# Revit family: 201_MAK+KL-_+TAK-___
name_source: partatom
category: Air Terminals
units: mm (PartAtom-declared; Revit-internal decimal feet)

## family parameters
Always vertical = Yes
Cut with Voids When Loaded = No
Part Type = Normal
Room Calculation Point = Yes
Round Connector Dimension = Use Diameter
Shared = No
Work Plane-Based = No

## types (4) — shared parameters
AA1 = 298 mm
AA2 = 298 mm
BOX0 = No
BOX1 = Yes
CAT0 = Yes
CAT1 = Yes
CAT2 = Yes
Description = Square nozzle diffuser with balancing plenum box
H4 = 8 mm  [stored 0.0262467 ft]
H4__ve = -8 mm  [stored -0.0262467 ft]
H5 = 10 mm  [stored 0.0328084 ft]
L_ARR = 400 mm
Manufacturer = Climecon
QmdConnectorList = 201;D
URL = www.climecon.fi
W_ARR = 400 mm
XRefLineVPlnId = 7453
YRefLineVPlnId = 7456
magiPartTypeId = 201
magiProductFamilyId = MAK+KL-*+TAK-*/*
zero-valued in all types: H_ARR, MC_Default_elevation

## per-type parameters (varying)
| type | B | B1 | B__ve | C | CLBTZ | CLBTZ_End__ve | CLBTZ__ve | CLD | CL_Location_5000 | D | D1 | H | H1 | H2 | H3 | H6 | R | R1 | R2 | W1 | WW1 |
| MAK+KL-125+TAK-100/125 | 450 mm | 358 mm | -450 mm  [stored -1.47638 ft] | 92 mm  [stored 0.301837 ft] | 30 mm  [stored 0.0984252 ft] | -40 mm  [stored -0.131234 ft] | -30 mm  [stored -0.0984252 ft] | 125 mm  [stored 0.410105 ft] | 5030 mm | 100 mm | 340 mm | 140 mm  [stored 0.459318 ft] | 40 mm  [stored 0.131234 ft] | 33 mm | 107 mm | 70 mm  [stored 0.229659 ft] | 50 mm  [stored 0.164042 ft] | 132 mm | 170 mm  [stored 0.557743 ft] | 135 mm  [stored 0.442913 ft] | 103 mm |
| MAK+KL-250+TAK-200/250 | 570 mm | 415 mm | -570 mm  [stored -1.87008 ft] | 155 mm  [stored 0.50853 ft] | 50 mm  [stored 0.164042 ft] | -60 mm | -50 mm  [stored -0.164042 ft] | 250 mm | 5050 mm | 200 mm | 520 mm | 240 mm | 60 mm  [stored 0.19685 ft] | 49 mm | 192 mm | 120 mm  [stored 0.393701 ft] | 100 mm  [stored 0.328084 ft] | 208 mm | 260 mm | 200 mm | 152 mm  [stored 0.498688 ft] |
| MAK+KL-200+TAK-160/200 | 500 mm | 370 mm | -500 mm  [stored -1.64042 ft] | 130 mm  [stored 0.426509 ft] | 40 mm  [stored 0.131234 ft] | -50 mm  [stored -0.164042 ft] | -40 mm  [stored -0.131234 ft] | 200 mm | 5040 mm | 160 mm | 430 mm | 200 mm | 50 mm  [stored 0.164042 ft] | 41 mm | 159 mm | 100 mm  [stored 0.328084 ft] | 80 mm  [stored 0.262467 ft] | 170 mm  [stored 0.557743 ft] | 215 mm | 170 mm  [stored 0.557743 ft] | 129 mm |
| MAK+KL-160+TAK-125/160 | 450 mm | 340 mm | -450 mm  [stored -1.47638 ft] | 110 mm  [stored 0.360892 ft] | 30 mm  [stored 0.0984252 ft] | -40 mm  [stored -0.131234 ft] | -30 mm  [stored -0.0984252 ft] | 160 mm  [stored 0.524934 ft] | 5030 mm | 125 mm | 340 mm | 165 mm  [stored 0.541339 ft] | 40 mm  [stored 0.131234 ft] | 33 mm | 132 mm | 83 mm | 63 mm | 132 mm | 170 mm  [stored 0.557743 ft] | 135 mm  [stored 0.442913 ft] | 103 mm |

note: column(s) folded — value = type name in every type: magiProductCode, magiProductId

note: [stored X ft] marks values corroborated as IEEE doubles in the binary element streams (Revit-internal decimal feet)
